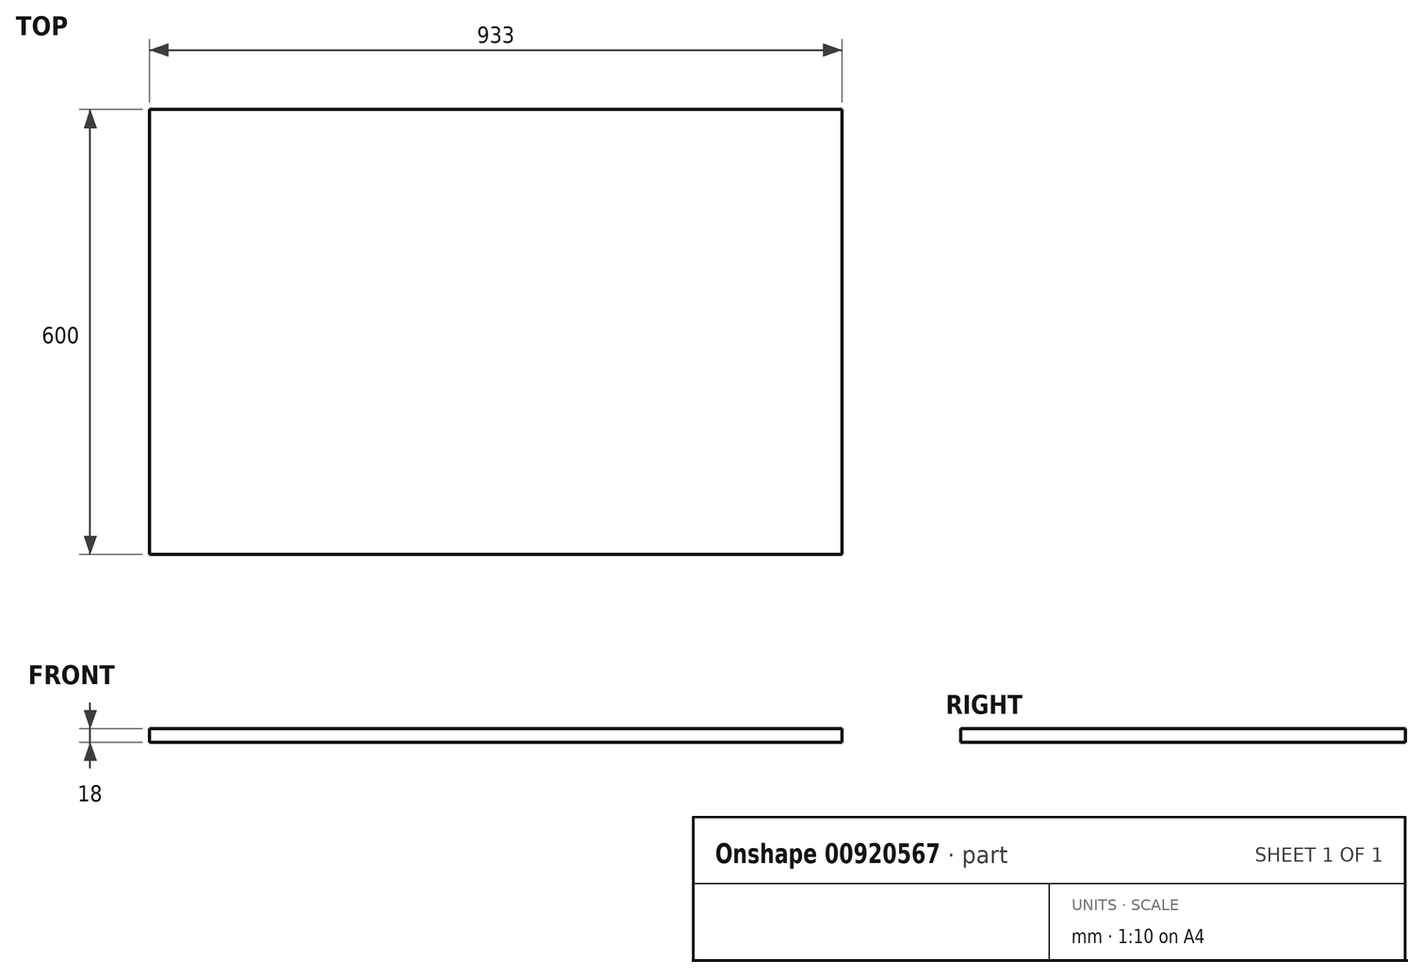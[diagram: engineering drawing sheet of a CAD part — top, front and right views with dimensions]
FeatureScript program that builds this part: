
annotation { "Feature Type Name" : "Feature", "Feature Type Description" : "" }
export const myFeature = defineFeature(function(context is Context, id is Id, definition is map)
    precondition{}
    {
        {
            var Q0;
            Q0=qCreatedBy(makeId("Top.planeOp"),FACE);
            var sketch = newSketch(context, id + "F0", { "sketchPlane" : qUnion([Q0])});
            skLineSegment(sketch, "E0.bottom", {"start": v(466.5, -300) * mm, "end": v(-466.5, -300) * mm});
            skLineSegment(sketch, "E0.top", {"start": v(466.5, 300) * mm, "end": v(-466.5, 300) * mm});
            skLineSegment(sketch, "E0.left", {"start": v(466.5, -300) * mm, "end": v(466.5, 300) * mm});
            skLineSegment(sketch, "E0.right", {"start": v(-466.5, -300) * mm, "end": v(-466.5, 300) * mm});
            skPoint(sketch, "E0.middle", {"position": v(0, 0) * mm});
            skSolve(sketch);
        }
        {
            var Q0;
            Q0 = qSketchRegion(id + "F0", true);
            extrude(context, id + "F1", {"entities" : qUnion([Q0]), "depth" : 18 * mm, "offsetDistance" : 25 * mm, "symmetric" : true});
        }
    });
